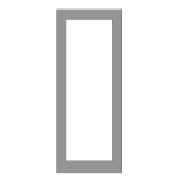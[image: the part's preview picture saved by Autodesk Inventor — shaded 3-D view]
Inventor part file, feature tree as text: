
AUTODESK INVENTOR PART (.ipt)
format: ipt  version: 2020 (Build 240168000, 168)  size: 190,464 bytes
history: native  units: in
note: dims shown in document units (in); Inventor stores cm internally (conversion verified against a paired STEP export)
features: sketch x5, other x4, plane x3, split x2, extrude x1, hole x1
ambient origin geometry x8: Origin, YZ Plane, XZ Plane, XY Plane, X Axis, Y Axis, Z Axis, Center Point
bodies: Solid1 (feature_tree), Body (feature_tree)
feature tree (16):
  other  "Driven Length"
  other  "Frame Generator"
  other  "Start Plane"
  other  "End Plane"
  plane  "Work Plane6"
  split  "Split1"
  plane  "Work Plane7"
  split  "Split2"
  extrude  "Extrusion3"  Depth=3.0in
  hole  "Hole1"  [1 undecoded]
  sketch  "Sketch"  dims[d8=0.13in d9=0.0in d14=90.0deg d11=30.0in d16=1.125in d18=1.0in d19=0.0in d21=0.5in d22=0.5in d23=0.7874in d25=28.0in d26=0.7874in d28=2.0in d31=0.196in d32=0.75in d33=0.385in d34=0.25in d35=0.5635in d36=1.0in d37=0.8108in d44=0.3135in d45=0.3135in d46=3.5in d47=3.5in d48=2.0in d49=2.0in d50=1.25in d51=1.25in d52=1.125in]
  sketch  "Sketch6"  dims[d0=1.0in d1=3.0in]
  plane  "Work Plane5"
  sketch  "Sketch7"  dims[d2=0.125in d3=0.125in]
  sketch  "Sketch8"  dims[d6=-0.5in]
  sketch  "Sketch9"  dims[d7=29.5in]
note: 1 required parameter value undecoded (feature->parameter linkage not recoverable at this tier; creation-order binding heuristic only, values carry confidence <= 0.55)
